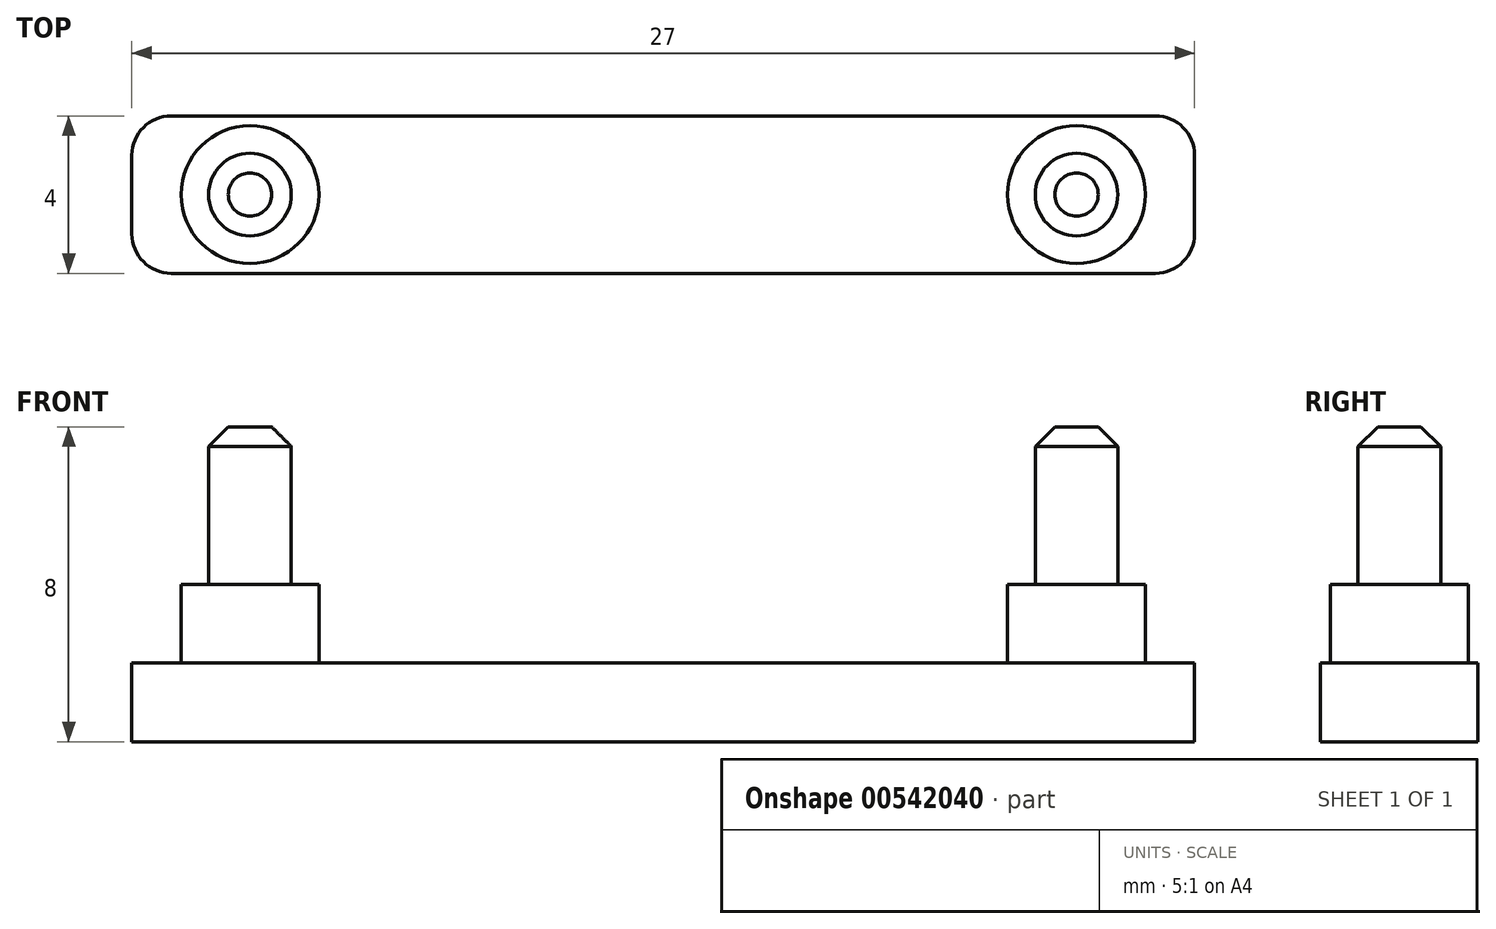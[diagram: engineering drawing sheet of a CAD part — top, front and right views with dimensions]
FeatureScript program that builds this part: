
annotation { "Feature Type Name" : "Feature", "Feature Type Description" : "" }
export const myFeature = defineFeature(function(context is Context, id is Id, definition is map)
    precondition{}
    {
        {
            var Q0;
            Q0=qCreatedBy(makeId("Top.planeOp"),FACE);
            var sketch = newSketch(context, id + "F0", { "sketchPlane" : qUnion([Q0])});
            skLineSegment(sketch, "E0.bottom", {"start": v(13.5, -2) * mm, "end": v(-13.5, -2) * mm});
            skLineSegment(sketch, "E0.top", {"start": v(13.5, 2) * mm, "end": v(-13.5, 2) * mm});
            skLineSegment(sketch, "E0.left", {"start": v(13.5, -2) * mm, "end": v(13.5, 2) * mm});
            skLineSegment(sketch, "E0.right", {"start": v(-13.5, -2) * mm, "end": v(-13.5, 2) * mm});
            skPoint(sketch, "E0.middle", {"position": v(0, 0) * mm});
            skSolve(sketch);
        }
        {
            var Q0;
            Q0 = qSketchRegion(id + "F0", true);
            extrude(context, id + "F1", {"entities" : qUnion([Q0]), "depth" : 2 * mm, "offsetDistance" : 25 * mm});
        }
        {
            var Q0;
            Q0=makeQuery(id+"F1.opExtrude","CAP_FACE",FACE,{"disambiguationData":[OSD([sQuery(id+"F0.wireOp",EDGE,"E0.bottom"),sQuery(id+"F0.wireOp",EDGE,"E0.top"),sQuery(id+"F0.wireOp",EDGE,"E0.left"),sQuery(id+"F0.wireOp",EDGE,"E0.right")])],"isStart":false});
            var sketch = newSketch(context, id + "F2", { "sketchPlane" : qUnion([Q0])});
            skCircle(sketch, "E1", {"center": v(-10.5, 0) * mm, "radius": 1.05 * mm});
            skCircle(sketch, "E2", {"center": v(10.5, 0) * mm, "radius": 1.05 * mm});
            skLineSegment(sketch, "E3", {"start": v(-10.5, 0) * mm, "end": v(10.5, 0) * mm});
            skSolve(sketch);
        }
        {
            var Q0;
            Q0 = qSketchRegion(id + "F2", true);
            extrude(context, id + "F3", {"entities" : qUnion([Q0]), "operationType" : NewBodyOperationType.ADD, "depth" : 6 * mm, "offsetDistance" : 25 * mm});
        }
        {
            var Q0;
            Q0=makeQuery(id+"F3.opExtrude","CAP_EDGE",EDGE,{"disambiguationData":[OSD([sQuery(id+"F2.wireOp",EDGE,"E1")])],"isStart":false});
            var Q1;
            Q1=makeQuery(id+"F3.opExtrude","CAP_EDGE",EDGE,{"disambiguationData":[OSD([sQuery(id+"F2.wireOp",EDGE,"E2")])],"isStart":false});
            chamfer(context, id + "F4", {"entities" : qUnion([Q0, Q1]), "width" : 0.5 * mm, "tangentPropagation" : true});
        }
        {
            var Q0;
            Q0=makeQuery(id+"F1.opExtrude","SWEPT_EDGE",EDGE,{"disambiguationData":[OSD([sQuery(id+"F0.wireOp",EDGE,"E0.bottom"),sQuery(id+"F0.wireOp",EDGE,"E0.right")])]});
            var Q1;
            Q1=makeQuery(id+"F1.opExtrude","SWEPT_EDGE",EDGE,{"disambiguationData":[OSD([sQuery(id+"F0.wireOp",EDGE,"E0.top"),sQuery(id+"F0.wireOp",EDGE,"E0.right")])]});
            var Q2;
            Q2=makeQuery(id+"F1.opExtrude","SWEPT_EDGE",EDGE,{"disambiguationData":[OSD([sQuery(id+"F0.wireOp",EDGE,"E0.top"),sQuery(id+"F0.wireOp",EDGE,"E0.left")])]});
            var Q3;
            Q3=makeQuery(id+"F1.opExtrude","SWEPT_EDGE",EDGE,{"disambiguationData":[OSD([sQuery(id+"F0.wireOp",EDGE,"E0.bottom"),sQuery(id+"F0.wireOp",EDGE,"E0.left")])]});
            fillet(context, id + "F5", {"entities" : qUnion([Q0, Q1, Q2, Q3]), "radius" : 1 * mm, "tangentPropagation" : true, "allowEdgeOverflow" : false});
        }
        {
            var Q0;
            Q0=makeQuery(id+"F1.opExtrude","CAP_FACE",FACE,{"disambiguationData":[OSD([sQuery(id+"F0.wireOp",EDGE,"E0.bottom"),sQuery(id+"F0.wireOp",EDGE,"E0.top"),sQuery(id+"F0.wireOp",EDGE,"E0.left"),sQuery(id+"F0.wireOp",EDGE,"E0.right")])],"isStart":false});
            var sketch = newSketch(context, id + "F6", { "sketchPlane" : qUnion([Q0])});
            skCircle(sketch, "E4.0", {"center": v(-10.5, 0) * mm, "radius": 1.75 * mm});
            skCircle(sketch, "E5.0", {"center": v(10.5, 0) * mm, "radius": 1.75 * mm});
            skSolve(sketch);
        }
        {
            var Q0;
            Q0 = qSketchRegion(id + "F6", true);
            extrude(context, id + "F7", {"entities" : qUnion([Q0]), "operationType" : NewBodyOperationType.ADD, "depth" : 2 * mm, "offsetDistance" : 25 * mm});
        }
    });
